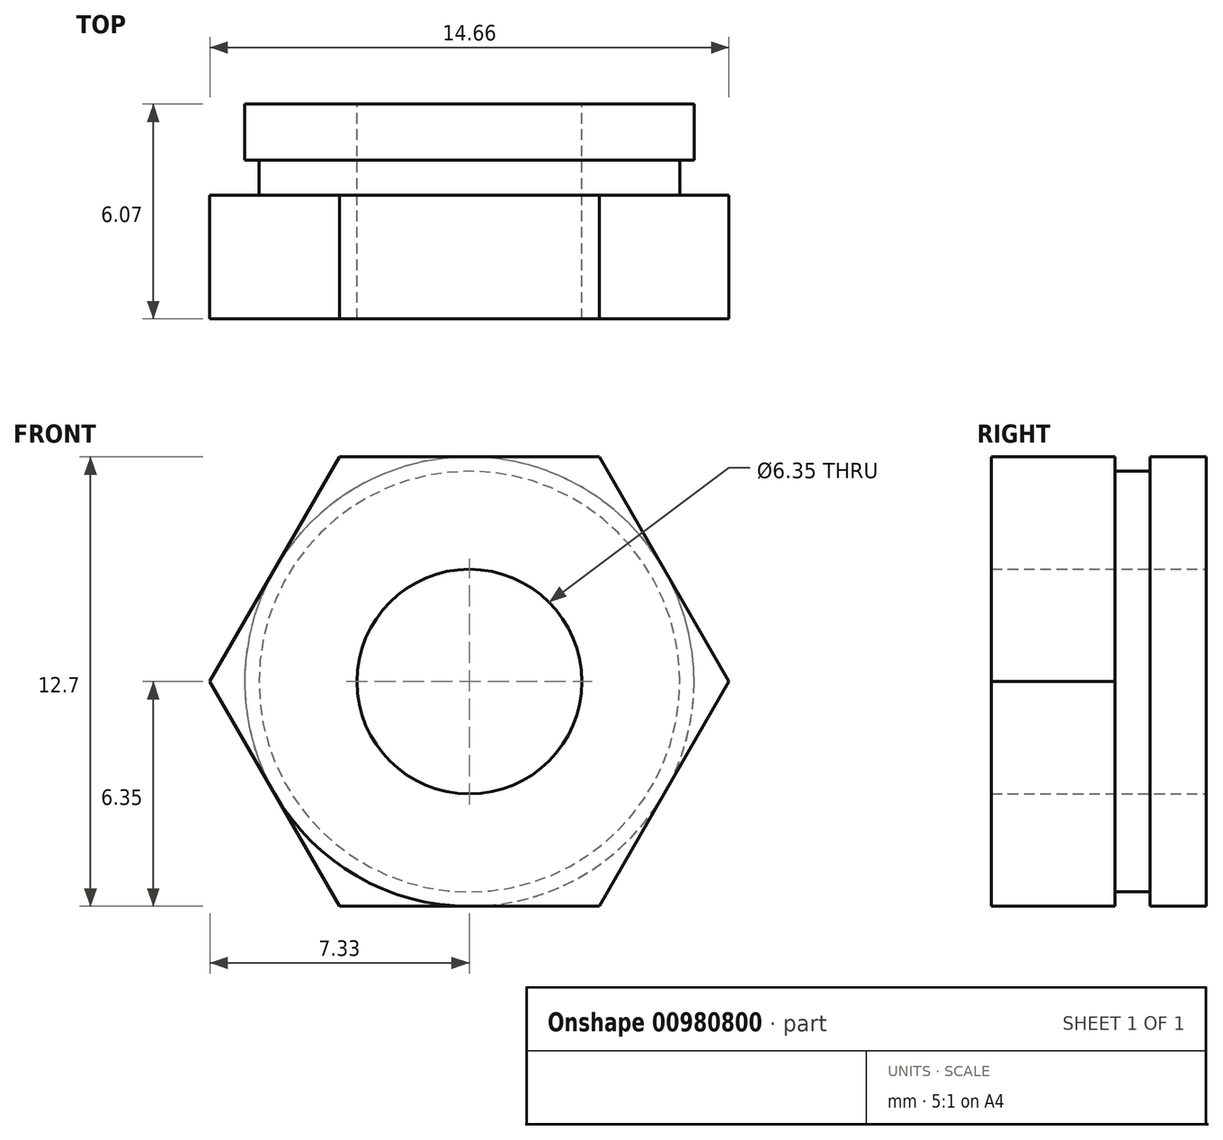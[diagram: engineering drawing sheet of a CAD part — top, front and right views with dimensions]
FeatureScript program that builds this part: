
annotation { "Feature Type Name" : "Feature", "Feature Type Description" : "" }
export const myFeature = defineFeature(function(context is Context, id is Id, definition is map)
    precondition{}
    {
        {
            var Q0;
            Q0=qCreatedBy(makeId("Front.planeOp"),FACE);
            var sketch = newSketch(context, id + "F0", { "sketchPlane" : qUnion([Q0])});
            skCircle(sketch, "E0", {"center": v(0, 0) * mm, "radius": 3.18 * mm});
            skCircle(sketch, "E1.cCircle", {"center": v(0, 0) * mm, "radius": 6.35 * mm, "construction": true});
            skLineSegment(sketch, "E1.0", {"start": v(-3.67, 6.35) * mm, "end": v(3.67, 6.35) * mm});
            skLineSegment(sketch, "E1.1", {"start": v(3.67, 6.35) * mm, "end": v(7.33, 0) * mm});
            skLineSegment(sketch, "E1.2", {"start": v(7.33, 0) * mm, "end": v(3.67, -6.35) * mm});
            skLineSegment(sketch, "E1.3", {"start": v(3.67, -6.35) * mm, "end": v(-3.67, -6.35) * mm});
            skLineSegment(sketch, "E1.4", {"start": v(-3.67, -6.35) * mm, "end": v(-7.33, 0) * mm});
            skLineSegment(sketch, "E1.5", {"start": v(-7.33, 0) * mm, "end": v(-3.67, 6.35) * mm});
            skPoint(sketch, "E1.0.midPoint", {"position": v(0, 6.35) * mm});
            skSolve(sketch);
        }
        {
            var Q0;
            Q0 = qSketchRegion(id + "F0", true);
            extrude(context, id + "F1", {"entities" : qUnion([Q0]), "depth" : (((6.38 - 0.03 + .39 + .625) - 0.02) - 1.26) * mm, "offsetDistance" : 25.4 * mm});
        }
        {
            var Q0;
            Q0=qCreatedBy(makeId("Top.planeOp"),FACE);
            var sketch = newSketch(context, id + "F2", { "sketchPlane" : qUnion([Q0])});
            skLineSegment(sketch, "E2", {"start": v(6.35, 0) * mm, "end": v(6.35, -1.59) * mm});
            skLineSegment(sketch, "E3", {"start": v(6.35, -1.59) * mm, "end": v(5.94, -1.59) * mm});
            skLineSegment(sketch, "E4", {"start": v(5.94, -1.59) * mm, "end": v(5.94, -2.58) * mm});
            skLineSegment(sketch, "E5", {"start": v(5.94, -2.58) * mm, "end": v(7.33, -2.58) * mm});
            skLineSegment(sketch, "E6", {"start": v(7.33, -2.58) * mm, "end": v(7.33, 0) * mm});
            skLineSegment(sketch, "E7", {"start": v(7.33, 0) * mm, "end": v(6.35, 0) * mm});
            skLineSegment(sketch, "E8", {"start": v(0, 0) * mm, "end": v(0, -2.58) * mm, "construction": true});
            skLineSegment(sketch, "E9", {"start": v(-3.67, -65.5) * mm, "end": v(3.67, -65.5) * mm, "construction": true});
            skLineSegment(sketch, "E10", {"start": v(0, 0) * mm, "end": v(0, -65.5) * mm, "construction": true});
            skLineSegment(sketch, "E11", {"start": v(0, -131) * mm, "end": v(0, -65.5) * mm, "construction": true});
            skLineSegment(sketch, "E12.MirrorCS", {"start": v(5.94, -128.41) * mm, "end": v(7.33, -128.41) * mm});
            skLineSegment(sketch, "E13.MirrorCS", {"start": v(7.33, -131) * mm, "end": v(6.35, -131) * mm});
            skLineSegment(sketch, "E14.MirrorCS", {"start": v(6.35, -131) * mm, "end": v(6.35, -129.4) * mm});
            skLineSegment(sketch, "E15.MirrorCS", {"start": v(5.94, -129.4) * mm, "end": v(5.94, -128.41) * mm});
            skLineSegment(sketch, "E16.MirrorCS", {"start": v(7.33, -128.41) * mm, "end": v(7.33, -131) * mm});
            skLineSegment(sketch, "E17.MirrorCS", {"start": v(6.35, -129.4) * mm, "end": v(5.94, -129.4) * mm});
            skLineSegment(sketch, "E18.MirrorCS", {"start": v(0, -131) * mm, "end": v(0, -128.41) * mm, "construction": true});
            skSolve(sketch);
        }
        {
            var Q0;
            Q0 = qSketchRegion(id + "F2", true);
            var Q1;
            Q1=sQuery(id+"F2.wireOp",EDGE,"E8");
            revolve(context, id + "F3", {"operationType" : NewBodyOperationType.REMOVE, "surfaceOperationType" : NewSurfaceOperationType.NEW, "entities" : qUnion([Q0]), "axis" : qUnion([Q1]), "revolveType" : RevolveType.FULL, "oppositeDirection" : true});
        }
    });
